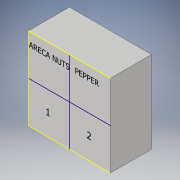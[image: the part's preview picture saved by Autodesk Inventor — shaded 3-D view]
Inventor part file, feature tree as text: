
AUTODESK INVENTOR PART (.ipt)
format: ipt  version: 2019 (Build 230136000, 136)  size: 99,840 bytes
history: native  units: in
note: dims shown in document units (in); Inventor stores cm internally (conversion verified against a paired STEP export)
features: sketch x3, extrude x1
ambient origin geometry x8: Origin, YZ Plane, XZ Plane, XY Plane, X Axis, Y Axis, Z Axis, Center Point
bodies: Solid1 (feature_tree)
feature tree (4):
  extrude  "Extrusion1"  Depth=1.5748in
  sketch  "Sketch2"  dims[d2=0.7874in]
  sketch  "Sketch3"  dims[d3=0.7874in d4=0.7874in d5=0.0in]
  sketch  "Sketch1"  dims[d0=1.5748in d1=1.5748in]
